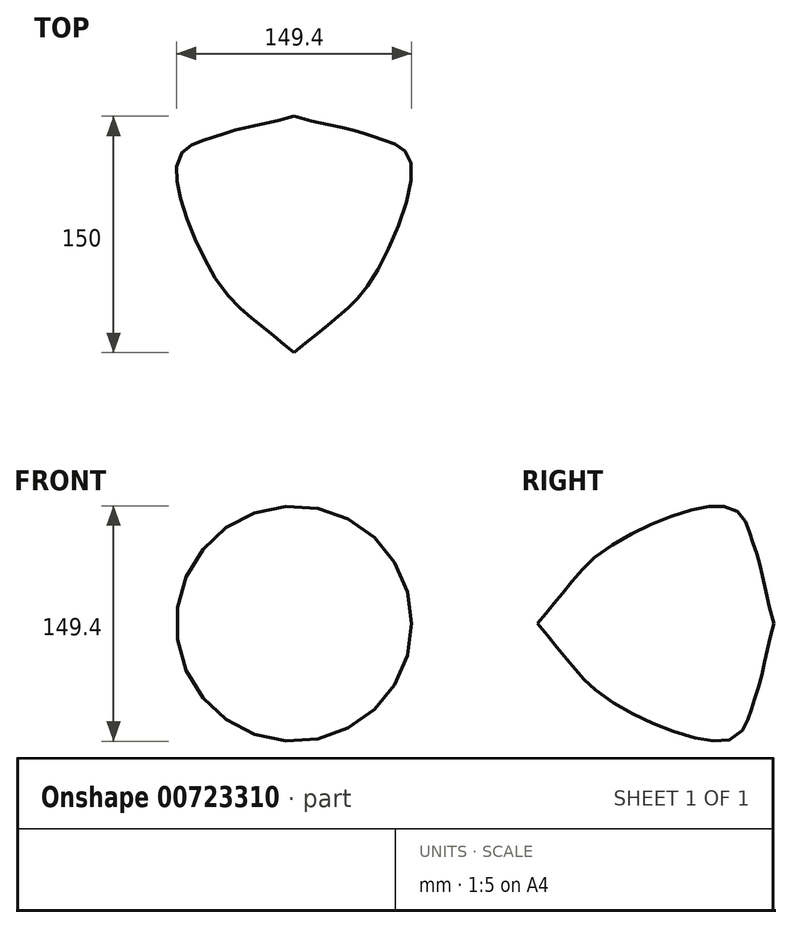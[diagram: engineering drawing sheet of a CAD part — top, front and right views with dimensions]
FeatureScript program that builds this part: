
annotation { "Feature Type Name" : "Feature", "Feature Type Description" : "" }
export const myFeature = defineFeature(function(context is Context, id is Id, definition is map)
    precondition{}
    {
        {
            var Q0;
            Q0=qCreatedBy(makeId("Top.planeOp"),FACE);
            var sketch = newSketch(context, id + "F0", { "sketchPlane" : qUnion([Q0])});
            skLineSegment(sketch, "E0", {"start": v(0, 75) * mm, "end": v(0, -75) * mm});
            skFitSpline(sketch, "E1", {"points": [v(0, 75) * mm, v(38.75, 65.8) * mm, v(54.34, 60.76) * mm, v(73.6, 47.46) * mm, v(50.22, -27.29) * mm, v(26.37, -53.43) * mm, v(0, -75) * mm], "startDerivative": vector(266.66, -74.2) * mm, "endDerivative": vector(-168.25, -133.3) * mm});
            skSolve(sketch);
        }
        {
            var Q0;
            Q0 = qSketchRegion(id + "F0", true);
            var Q1;
            Q1=sQuery(id+"F0.wireOp",EDGE,"E0");
            revolve(context, id + "F1", {"surfaceOperationType" : NewSurfaceOperationType.NEW, "entities" : qUnion([Q0]), "axis" : qUnion([Q1]), "revolveType" : RevolveType.FULL});
        }
    });
